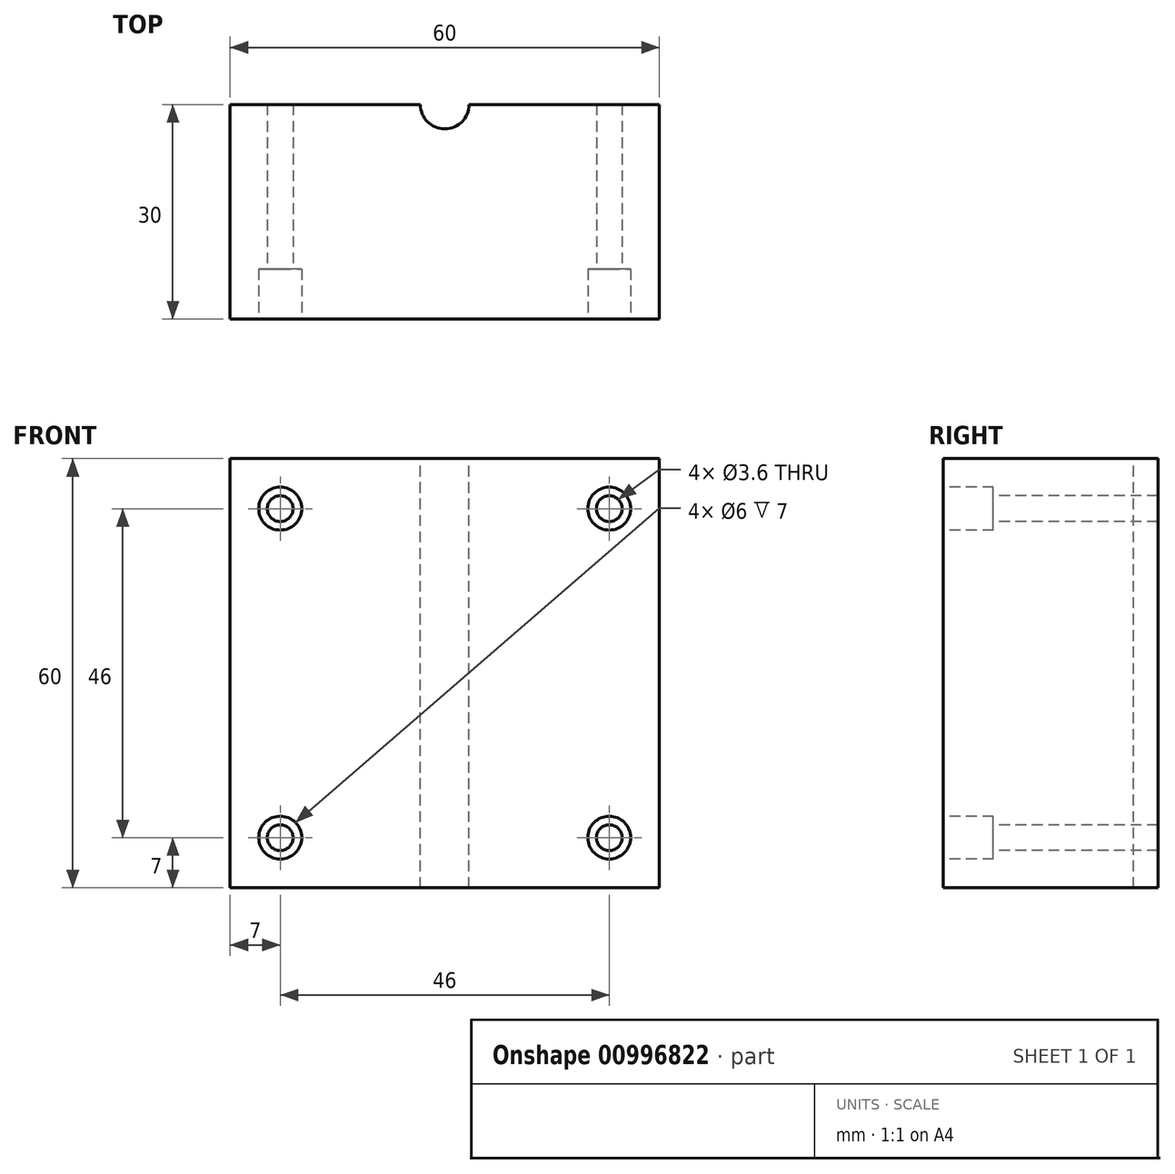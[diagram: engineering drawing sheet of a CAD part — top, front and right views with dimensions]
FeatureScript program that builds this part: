
annotation { "Feature Type Name" : "Feature", "Feature Type Description" : "" }
export const myFeature = defineFeature(function(context is Context, id is Id, definition is map)
    precondition{}
    {
        {
            var Q0;
            Q0=qCreatedBy(makeId("Top.planeOp"),FACE);
            var sketch = newSketch(context, id + "F0", { "sketchPlane" : qUnion([Q0])});
            skLineSegment(sketch, "E0.bottom", {"start": v(30, -15) * mm, "end": v(-30, -15) * mm});
            skLineSegment(sketch, "E0.top", {"start": v(30, 15) * mm, "end": v(-30, 15) * mm});
            skLineSegment(sketch, "E0.left", {"start": v(30, -15) * mm, "end": v(30, 15) * mm});
            skLineSegment(sketch, "E0.right", {"start": v(-30, -15) * mm, "end": v(-30, 15) * mm});
            skPoint(sketch, "E0.middle", {"position": v(0, 0) * mm});
            skSolve(sketch);
        }
        {
            var Q0;
            Q0 = qSketchRegion(id + "F0", true);
            extrude(context, id + "F1", {"entities" : qUnion([Q0]), "depth" : 60 * mm, "offsetDistance" : 25 * mm});
        }
        {
            var Q0;
            Q0=makeQuery(id+"F1.opExtrude","CAP_FACE",FACE,{"disambiguationData":[OSD([sQuery(id+"F0.wireOp",EDGE,"E0.bottom"),sQuery(id+"F0.wireOp",EDGE,"E0.top"),sQuery(id+"F0.wireOp",EDGE,"E0.left"),sQuery(id+"F0.wireOp",EDGE,"E0.right")])],"isStart":false});
            var sketch = newSketch(context, id + "F2", { "sketchPlane" : qUnion([Q0])});
            skPoint(sketch, "E1", {"position": v(0, 15) * mm});
            skCircle(sketch, "E2", {"center": v(0, 15) * mm, "radius": 3.4 * mm});
            skSolve(sketch);
        }
        {
            var Q0;
            Q0 = qSketchRegion(id + "F2", true);
            extrude(context, id + "F3", {"entities" : qUnion([Q0]), "operationType" : NewBodyOperationType.REMOVE, "endBound" : BoundingType.THROUGH_ALL, "oppositeDirection" : true, "depth" : 25 * mm, "offsetDistance" : 25 * mm});
        }
        {
            var Q0;
            Q0=makeQuery(id+"F1.opExtrude","SWEPT_FACE",FACE,{"disambiguationData":[OSD([sQuery(id+"F0.wireOp",EDGE,"E0.bottom")])]});
            var sketch = newSketch(context, id + "F4", { "sketchPlane" : qUnion([Q0])});
            skPoint(sketch, "E3", {"position": v(-23, 53) * mm});
            skPoint(sketch, "E4", {"position": v(23, 53) * mm});
            skPoint(sketch, "E5", {"position": v(23, 7) * mm});
            skPoint(sketch, "E6", {"position": v(-23, 7) * mm});
            skCircle(sketch, "E7", {"center": v(-23, 53) * mm, "radius": 1.8 * mm});
            skCircle(sketch, "E8", {"center": v(23, 53) * mm, "radius": 1.8 * mm});
            skCircle(sketch, "E9", {"center": v(23, 7) * mm, "radius": 1.8 * mm});
            skCircle(sketch, "E10", {"center": v(-23, 7) * mm, "radius": 1.8 * mm});
            skSolve(sketch);
        }
        {
            var Q0;
            Q0 = qSketchRegion(id + "F4", true);
            extrude(context, id + "F5", {"entities" : qUnion([Q0]), "operationType" : NewBodyOperationType.REMOVE, "endBound" : BoundingType.THROUGH_ALL, "oppositeDirection" : true, "depth" : 25 * mm, "offsetDistance" : 25 * mm});
        }
        {
            var Q0;
            Q0=makeQuery(id+"F1.opExtrude","SWEPT_FACE",FACE,{"disambiguationData":[OSD([sQuery(id+"F0.wireOp",EDGE,"E0.bottom")])]});
            var sketch = newSketch(context, id + "F6", { "sketchPlane" : qUnion([Q0])});
            skPoint(sketch, "E11", {"position": v(-23, 53) * mm});
            skPoint(sketch, "E12", {"position": v(-166.26, 40.54) * mm});
            skCircle(sketch, "E13", {"center": v(-23, 53) * mm, "radius": 3 * mm});
            skSolve(sketch);
        }
        {
            var Q0;
            Q0 = qSketchRegion(id + "F6", true);
            extrude(context, id + "F7", {"entities" : qUnion([Q0]), "operationType" : NewBodyOperationType.REMOVE, "oppositeDirection" : true, "depth" : 7 * mm, "offsetDistance" : 25 * mm});
        }
        {
            var Q0;
            Q0=makeQuery(id+"F1.opExtrude","SWEPT_FACE",FACE,{"disambiguationData":[OSD([sQuery(id+"F0.wireOp",EDGE,"E0.bottom")])]});
            var sketch = newSketch(context, id + "F8", { "sketchPlane" : qUnion([Q0])});
            skPoint(sketch, "E14", {"position": v(23, 53) * mm});
            skCircle(sketch, "E15", {"center": v(23, 53) * mm, "radius": 3 * mm});
            skSolve(sketch);
        }
        {
            var Q0;
            Q0 = qSketchRegion(id + "F8", true);
            extrude(context, id + "F9", {"entities" : qUnion([Q0]), "operationType" : NewBodyOperationType.REMOVE, "oppositeDirection" : true, "depth" : 7 * mm, "offsetDistance" : 25 * mm});
        }
        {
            var Q0;
            Q0=makeQuery(id+"F1.opExtrude","SWEPT_FACE",FACE,{"disambiguationData":[OSD([sQuery(id+"F0.wireOp",EDGE,"E0.bottom")])]});
            var sketch = newSketch(context, id + "F10", { "sketchPlane" : qUnion([Q0])});
            skPoint(sketch, "E16", {"position": v(-23, 7) * mm});
            skCircle(sketch, "E17", {"center": v(-23, 7) * mm, "radius": 3 * mm});
            skSolve(sketch);
        }
        {
            var Q0;
            Q0 = qSketchRegion(id + "F10", true);
            extrude(context, id + "F11", {"entities" : qUnion([Q0]), "operationType" : NewBodyOperationType.REMOVE, "oppositeDirection" : true, "depth" : 7 * mm, "offsetDistance" : 25 * mm});
        }
        {
            var Q0;
            Q0=makeQuery(id+"F1.opExtrude","SWEPT_FACE",FACE,{"disambiguationData":[OSD([sQuery(id+"F0.wireOp",EDGE,"E0.bottom")])]});
            var sketch = newSketch(context, id + "F12", { "sketchPlane" : qUnion([Q0])});
            skPoint(sketch, "E18", {"position": v(23, 7) * mm});
            skCircle(sketch, "E19", {"center": v(23, 7) * mm, "radius": 3 * mm});
            skSolve(sketch);
        }
        {
            var Q0;
            Q0 = qSketchRegion(id + "F12", true);
            extrude(context, id + "F13", {"entities" : qUnion([Q0]), "operationType" : NewBodyOperationType.REMOVE, "oppositeDirection" : true, "depth" : 7 * mm, "offsetDistance" : 25 * mm});
        }
    });
